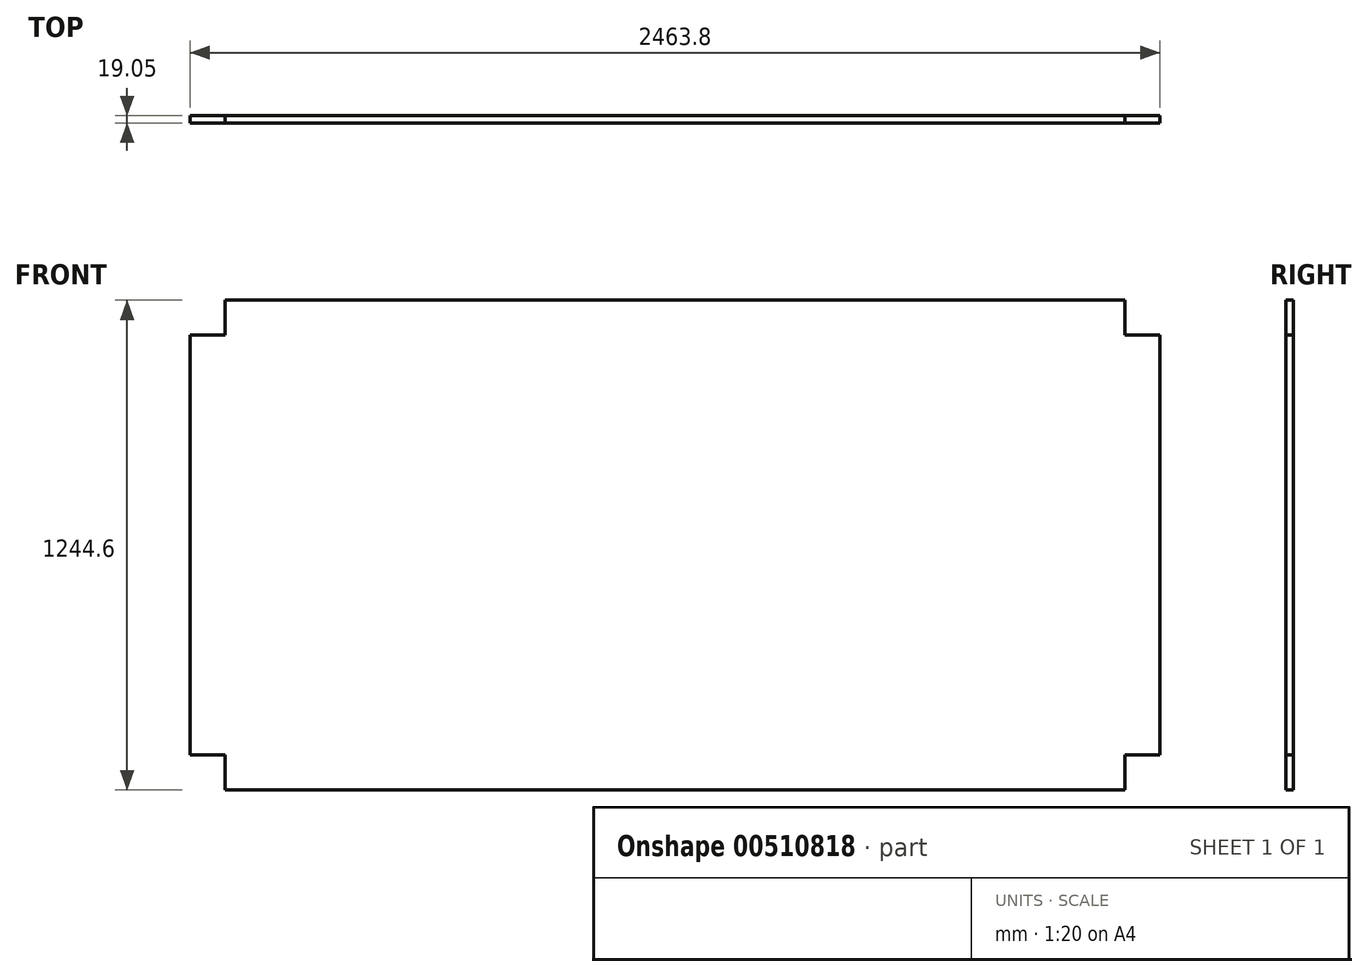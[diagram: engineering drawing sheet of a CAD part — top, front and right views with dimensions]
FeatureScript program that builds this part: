
annotation { "Feature Type Name" : "Feature", "Feature Type Description" : "" }
export const myFeature = defineFeature(function(context is Context, id is Id, definition is map)
    precondition{}
    {
        {
            var Q0;
            Q0=qCreatedBy(makeId("Front.planeOp"),FACE);
            var sketch = newSketch(context, id + "F0", { "sketchPlane" : qUnion([Q0])});
            skLineSegment(sketch, "E0", {"start": v(0, 622.3) * mm, "end": v(1231.9, 622.3) * mm});
            skLineSegment(sketch, "E1", {"start": v(1231.9, 622.3) * mm, "end": v(1231.9, 0) * mm});
            skLineSegment(sketch, "E2.MirrorCS", {"start": v(0, -622.3) * mm, "end": v(1231.9, -622.3) * mm});
            skLineSegment(sketch, "E3.MirrorCS", {"start": v(1231.9, -622.3) * mm, "end": v(1231.9, 0) * mm});
            skLineSegment(sketch, "E4.MirrorCS", {"start": v(-1231.9, -622.3) * mm, "end": v(-1231.9, 0) * mm});
            skLineSegment(sketch, "E5.MirrorCS", {"start": v(-1231.9, 622.3) * mm, "end": v(-1231.9, 0) * mm});
            skLineSegment(sketch, "E6.MirrorCS", {"start": v(0, -622.3) * mm, "end": v(-1231.9, -622.3) * mm});
            skLineSegment(sketch, "E7.MirrorCS", {"start": v(0, 622.3) * mm, "end": v(-1231.9, 622.3) * mm});
            skSolve(sketch);
        }
        {
            var Q0;
            Q0=qSketchRegion(id+"F0",true);
            extrude(context, id + "F1", {"entities" : qUnion([Q0]), "depth" : 19.05 * mm});
        }
        {
            var Q0;
            Q0=makeQuery(id+"F1.opExtrude","CAP_FACE",FACE,{"disambiguationData":[OSD([sQuery(id+"F0.wireOp",EDGE,"E0"),sQuery(id+"F0.wireOp",EDGE,"E1"),sQuery(id+"F0.wireOp",EDGE,"E2.MirrorCS"),sQuery(id+"F0.wireOp",EDGE,"E3.MirrorCS"),sQuery(id+"F0.wireOp",EDGE,"E4.MirrorCS"),sQuery(id+"F0.wireOp",EDGE,"E5.MirrorCS"),sQuery(id+"F0.wireOp",EDGE,"E6.MirrorCS"),sQuery(id+"F0.wireOp",EDGE,"E7.MirrorCS")])],"isStart":false});
            var sketch = newSketch(context, id + "F2", { "sketchPlane" : qUnion([Q0])});
            skLineSegment(sketch, "E8.bottom", {"start": v(-1231.9, 622.3) * mm, "end": v(-1143, 622.3) * mm});
            skLineSegment(sketch, "E8.top", {"start": v(-1231.9, 533.4) * mm, "end": v(-1143, 533.4) * mm});
            skLineSegment(sketch, "E8.left", {"start": v(-1231.9, 622.3) * mm, "end": v(-1231.9, 533.4) * mm});
            skLineSegment(sketch, "E8.right", {"start": v(-1143, 622.3) * mm, "end": v(-1143, 533.4) * mm});
            skLineSegment(sketch, "E9.MirrorCS", {"start": v(1143, 622.3) * mm, "end": v(1143, 533.4) * mm});
            skLineSegment(sketch, "E10.MirrorCS", {"start": v(1231.9, 622.3) * mm, "end": v(1231.9, 533.4) * mm});
            skLineSegment(sketch, "E11.MirrorCS", {"start": v(1231.9, 533.4) * mm, "end": v(1143, 533.4) * mm});
            skLineSegment(sketch, "E12.MirrorCS", {"start": v(1231.9, 622.3) * mm, "end": v(1143, 622.3) * mm});
            skLineSegment(sketch, "E13.MirrorCS", {"start": v(1231.9, -533.4) * mm, "end": v(1143, -533.4) * mm});
            skLineSegment(sketch, "E14.MirrorCS", {"start": v(1231.9, -622.3) * mm, "end": v(1231.9, -533.4) * mm});
            skLineSegment(sketch, "E15.MirrorCS", {"start": v(1143, -622.3) * mm, "end": v(1143, -533.4) * mm});
            skLineSegment(sketch, "E16.MirrorCS", {"start": v(-1143, -622.3) * mm, "end": v(-1143, -533.4) * mm});
            skLineSegment(sketch, "E17.MirrorCS", {"start": v(-1231.9, -622.3) * mm, "end": v(-1231.9, -533.4) * mm});
            skLineSegment(sketch, "E18.MirrorCS", {"start": v(-1231.9, -533.4) * mm, "end": v(-1143, -533.4) * mm});
            skLineSegment(sketch, "E19.MirrorCS", {"start": v(-1231.9, -622.3) * mm, "end": v(-1143, -622.3) * mm});
            skLineSegment(sketch, "E20.MirrorCS", {"start": v(1231.9, -622.3) * mm, "end": v(1143, -622.3) * mm});
            skSolve(sketch);
        }
        {
            var Q0;
            Q0=qSketchRegion(id+"F2",true);
            extrude(context, id + "F3", {"entities" : qUnion([Q0]), "operationType" : NewBodyOperationType.REMOVE, "oppositeDirection" : true, "depth" : 25.4 * mm});
        }
    });
